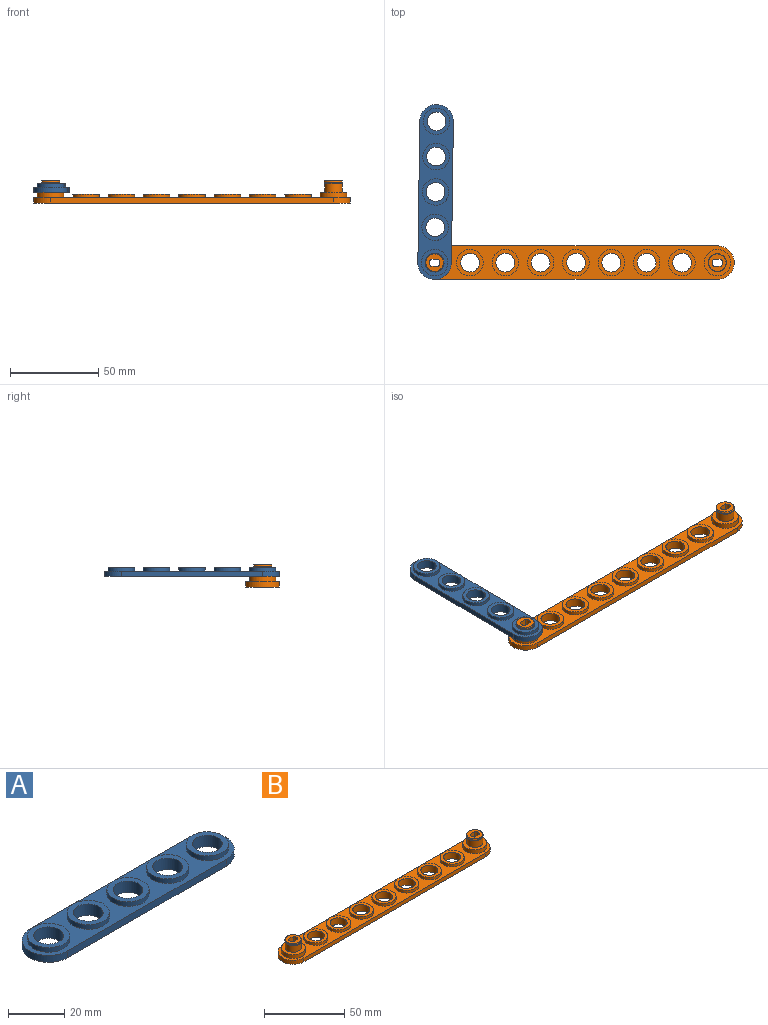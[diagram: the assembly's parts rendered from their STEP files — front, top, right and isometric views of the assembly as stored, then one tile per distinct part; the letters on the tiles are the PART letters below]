
ASSEMBLY  parts=2 mates=1
PART A: 21 faces, bbox 99x19x5 mm
  f0: cylinder r=9.5mm len=19mm, axis (0,0,-1), area 89.5mm2, adj f1,f6,f8,f9
  f1: plane 80x3mm, normal (0,1,0), area 240mm2, adj f0,f2,f8,f9
  f2: cylinder r=9.5mm len=19mm, axis (0,0,-1), area 89.5mm2, adj f1,f6,f8,f9
  f3: cylinder r=5.3mm len=10.6mm, axis (0,0,-1), area 166.5mm2, adj f9,f15
  f4: cylinder r=5.3mm len=10.6mm, axis (0,0,-1), area 166.5mm2, adj f9,f13
  f5: cylinder r=5.3mm len=10.6mm, axis (0,0,-1), area 166.5mm2, adj f9,f11
  f6: plane 80x3mm, normal (0,-1,0), area 240mm2, adj f0,f2,f8,f9
  f7: cylinder r=5.3mm len=10.6mm, axis (0,0,-1), area 166.5mm2, adj f9,f17
  f8: plane 99x19mm, normal (0,0,1), area 920mm2, adj f0,f1,f2,f6,f10,f12,f14,f16
  f9: plane 99x19mm, normal (0,0,-1), area 1362.3mm2, adj f0,f1,f2,f3,f4,f5,f6,f7
  f10: cylinder r=7.5mm len=15mm, axis (0,0,-1), area 94.2mm2, adj f8,f11
  f11: plane 15x15mm, normal (0,0,1), area 88.5mm2, adj f5,f10
  f12: cylinder r=7.5mm len=15mm, axis (0,0,-1), area 94.2mm2, adj f8,f13
  f13: plane 15x15mm, normal (0,0,1), area 88.5mm2, adj f4,f12
  f14: cylinder r=7.5mm len=15mm, axis (0,0,-1), area 94.2mm2, adj f8,f15
  f15: plane 15x15mm, normal (0,0,1), area 88.5mm2, adj f3,f14
  f16: cylinder r=7.5mm len=15mm, axis (0,0,-1), area 94.2mm2, adj f8,f17
  f17: plane 15x15mm, normal (0,0,1), area 88.5mm2, adj f7,f16
  f18: cylinder r=5.3mm len=10.6mm, axis (0,0,-1), area 166.5mm2, adj f9,f20
  f19: cylinder r=7.5mm len=15mm, axis (0,0,-1), area 94.2mm2, adj f8,f20
  f20: plane 15x15mm, normal (0,0,1), area 88.5mm2, adj f18,f19
PART B: 47 faces, bbox 179x19x12.5 mm
  f0: cylinder r=9.5mm len=19mm, axis (0,0,-1), area 89.5mm2, adj f1,f5,f7,f8
  f1: plane 160x3mm, normal (0,1,0), area 480mm2, adj f0,f2,f7,f8
  f2: cylinder r=9.5mm len=19mm, axis (0,0,-1), area 89.5mm2, adj f1,f5,f7,f8
  f3: cylinder r=5.3mm len=10.6mm, axis (0,0,-1), area 166.5mm2, adj f8,f13
  f4: cylinder r=5.3mm len=10.6mm, axis (0,0,-1), area 166.5mm2, adj f8,f11
  f5: plane 160x3mm, normal (0,-1,0), area 480mm2, adj f0,f2,f7,f8
  f6: cylinder r=5.3mm len=10.6mm, axis (0,0,-1), area 166.5mm2, adj f8,f15
  f7: plane 179x19mm, normal (0,0,1), area 1733.1mm2, adj f0,f1,f2,f5,f9,f10,f12,f14
  f8: plane 179x19mm, normal (0,0,-1), area 2661.7mm2, adj f0,f1,f2,f3,f4,f5,f6,f16
  f9: cylinder r=7.5mm len=15mm, axis (0,0,-1), area 141.4mm2, adj f7,f34
  f10: cylinder r=7.5mm len=15mm, axis (0,0,-1), area 94.2mm2, adj f7,f11
  f11: plane 15x15mm, normal (0,0,1), area 88.5mm2, adj f4,f10
  f12: cylinder r=7.5mm len=15mm, axis (0,0,-1), area 94.2mm2, adj f7,f13
  f13: plane 15x15mm, normal (0,0,1), area 88.5mm2, adj f3,f12
  f14: cylinder r=7.5mm len=15mm, axis (0,0,-1), area 94.2mm2, adj f7,f15
  f15: plane 15x15mm, normal (0,0,1), area 88.5mm2, adj f6,f14
  f16: cylinder r=5.3mm len=10.6mm, axis (0,0,-1), area 166.5mm2, adj f8,f18
  f17: cylinder r=7.5mm len=15mm, axis (0,0,-1), area 94.2mm2, adj f7,f18
  f18: plane 15x15mm, normal (0,0,1), area 88.5mm2, adj f16,f17
  f19: cylinder r=5.3mm len=10.6mm, axis (0,0,-1), area 166.5mm2, adj f8,f21
  f20: cylinder r=7.5mm len=15mm, axis (0,0,-1), area 94.2mm2, adj f7,f21
  f21: plane 15x15mm, normal (0,0,1), area 88.5mm2, adj f19,f20
  f22: cylinder r=5.3mm len=10.6mm, axis (0,0,-1), area 166.5mm2, adj f8,f24
  f23: cylinder r=7.5mm len=15mm, axis (0,0,-1), area 94.2mm2, adj f7,f24
  f24: plane 15x15mm, normal (0,0,1), area 88.5mm2, adj f22,f23
  f25: cylinder r=5.3mm len=10.6mm, axis (0,0,-1), area 166.5mm2, adj f8,f27
  f26: cylinder r=7.5mm len=15mm, axis (0,0,-1), area 94.2mm2, adj f7,f27
  f27: plane 15x15mm, normal (0,0,1), area 88.5mm2, adj f25,f26
  f28: cylinder r=7.5mm len=15mm, axis (0,0,-1), area 141.4mm2, adj f7,f43
  f29: cylinder r=4.95mm len=9.9mm, axis (0,0,-1), area 155.5mm2, adj f34,f36
  f30: cylinder r=2.95mm len=12.5mm, axis (0,0,-1), area 56.7mm2, adj f8,f31,f33,f35
  f31: plane 12.5x4.24mm, normal (0,-1,0), area 53mm2, adj f8,f30,f32,f35
  f32: cylinder r=2.95mm len=12.5mm, axis (0,0,-1), area 56.7mm2, adj f8,f31,f33,f35
  f33: plane 12.5x4.24mm, normal (0,1,0), area 53mm2, adj f8,f30,f32,f35
  f34: plane 15x15mm, normal (0,0,1), area 99.7mm2, adj f9,f29
  f35: plane 9.9x9.9mm, normal (0,0,1), area 54.9mm2, adj f30,f31,f32,f33,f37
  f36: cone r=5.2mm half-angle=18.4deg, axis (0,0,1), area 25.2mm2, adj f29,f37
  f37: cone r=4.95mm half-angle=18.4deg, axis (0,0,-1), area 25.2mm2, adj f35,f36
  f38: cylinder r=4.95mm len=9.9mm, axis (0,0,-1), area 155.5mm2, adj f43,f45
  f39: cylinder r=2.95mm len=12.5mm, axis (0,0,-1), area 56.7mm2, adj f8,f40,f42,f44
  f40: plane 12.5x4.24mm, normal (0,-1,0), area 53mm2, adj f8,f39,f41,f44
  f41: cylinder r=2.95mm len=12.5mm, axis (0,0,-1), area 56.7mm2, adj f8,f40,f42,f44
  f42: plane 12.5x4.24mm, normal (0,1,0), area 53mm2, adj f8,f39,f41,f44
  f43: plane 15x15mm, normal (0,0,1), area 99.7mm2, adj f28,f38
  f44: plane 9.9x9.9mm, normal (0,0,1), area 54.9mm2, adj f39,f40,f41,f42,f46
  f45: cone r=5.2mm half-angle=18.4deg, axis (0,0,1), area 25.2mm2, adj f38,f46
  f46: cone r=4.95mm half-angle=18.4deg, axis (0,0,-1), area 25.2mm2, adj f44,f45
PLACE A rot(axis=(0,0,1),89.2deg) t=(-84.27,-5.48,-16.01)mm
PLACE B t=(-84.27,-5.48,-22.01)mm fixed
MATE revolute A.f5 <-> B.f29  axis (0,0,-1) through (-84.27,-5.48,-16.01)mm
